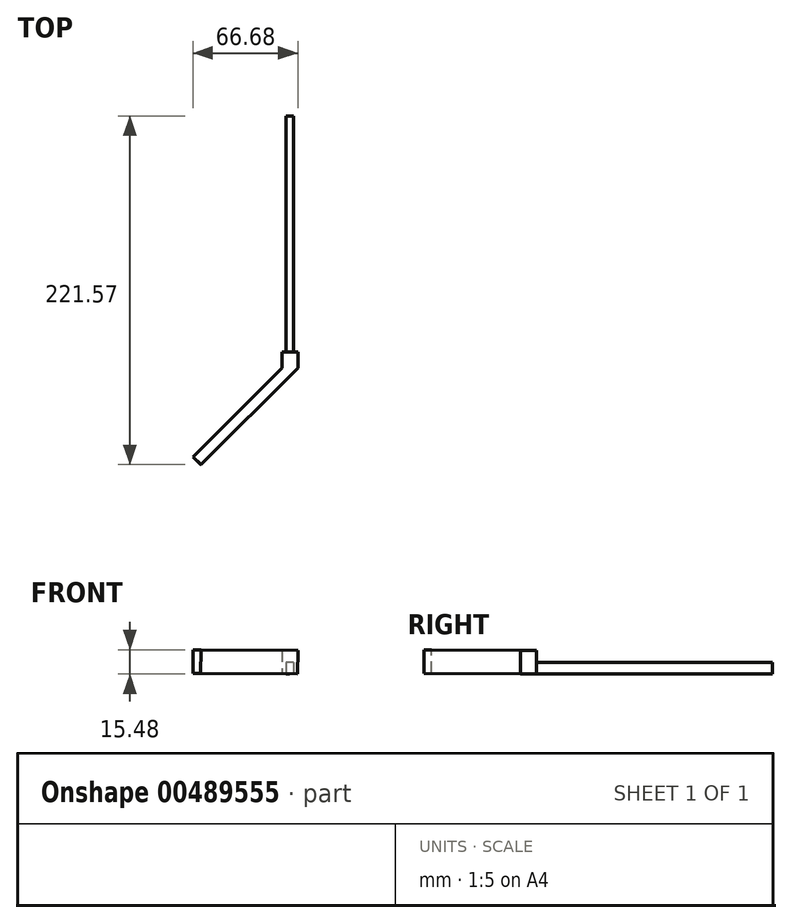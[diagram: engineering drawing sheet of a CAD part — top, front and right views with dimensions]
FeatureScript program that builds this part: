
annotation { "Feature Type Name" : "Feature", "Feature Type Description" : "" }
export const myFeature = defineFeature(function(context is Context, id is Id, definition is map)
    precondition{}
    {
        {
            var Q0;
            Q0=qCreatedBy(makeId("Top.planeOp"),FACE);
            var sketch = newSketch(context, id + "F0", { "sketchPlane" : qUnion([Q0])});
            skLineSegment(sketch, "E0.bottom", {"start": v(2.25, 75) * mm, "end": v(-2.25, 75) * mm});
            skLineSegment(sketch, "E0.top", {"start": v(2.25, -75) * mm, "end": v(-2.25, -75) * mm});
            skLineSegment(sketch, "E0.left", {"start": v(2.25, 75) * mm, "end": v(2.25, -75) * mm});
            skLineSegment(sketch, "E0.right", {"start": v(-2.25, 75) * mm, "end": v(-2.25, -75) * mm});
            skPoint(sketch, "E0.middle", {"position": v(0, 0) * mm});
            skSolve(sketch);
        }
        {
            var Q0;
            Q0 = qSketchRegion(id + "F0", true);
            extrude(context, id + "F1", {"entities" : qUnion([Q0]), "depth" : 7.3 * mm});
        }
        {
            var Q0;
            Q0=makeQuery(id+"F1.opExtrude","SWEPT_FACE",FACE,{"disambiguationData":[OSD([sQuery(id+"F0.wireOp",EDGE,"E0.top")])]});
            var sketch = newSketch(context, id + "F2", { "sketchPlane" : qUnion([Q0])});
            skLineSegment(sketch, "E1.bottom", {"start": v(5.1, 14.96) * mm, "end": v(-4.9, 15.04) * mm});
            skLineSegment(sketch, "E1.left", {"start": v(5.1, 14.96) * mm, "end": v(5, -0.04) * mm});
            skLineSegment(sketch, "E1.right", {"start": v(-4.9, 15.04) * mm, "end": v(-5, 0.04) * mm});
            skPoint(sketch, "E1.middle", {"position": v(0, 0) * mm});
            skLineSegment(sketch, "E2", {"start": v(-5, 0.04) * mm, "end": v(5, -0.04) * mm});
            skPoint(sketch, "E1.top.end.orphan", {"position": v(-5.1, -14.96) * mm});
            skPoint(sketch, "E1.top.start.orphan", {"position": v(4.9, -15.04) * mm});
            skSolve(sketch);
        }
        {
            var Q0;
            {var subQ0=sQuery(id+"F0.wireOp",EDGE,"E0.top");var subQ1=makeQuery(id+"F1.opExtrude","CAP_EDGE",EDGE,{"disambiguationData":[OSD([subQ0])],"isStart":false});Q0=makeQuery(id+"F2.imprint","IMPRINT",FACE,{"disambiguationData":[TD([[makeQuery(id+"F2.imprint","IMPRINT",EDGE,{"derivedFrom":subQ1}),1.0]])]});}
            var Q1;
            Q1=makeQuery(id+"F2.imprint","IMPRINT",FACE,{"disambiguationData":[TD([[makeQuery(id+"F2.imprint","IMPRINT",EDGE,{"derivedFrom":sQuery(id+"F2.wireOp",EDGE,"E1.bottom")}),1.0]])]});
            extrude(context, id + "F3", {"entities" : qUnion([Q0, Q1]), "operationType" : NewBodyOperationType.ADD, "depth" : 10 * mm});
        }
        {
            var Q0;
            Q0=makeQuery(id+"F3.opExtrude","SWEPT_FACE",FACE,{"disambiguationData":[OSD([sQuery(id+"F2.wireOp",EDGE,"E1.bottom")])]});
            var sketch = newSketch(context, id + "F4", { "sketchPlane" : qUnion([Q0])});
            skLineSegment(sketch, "E3", {"start": v(-5, -85) * mm, "end": v(-61.57, -141.57) * mm});
            skLineSegment(sketch, "E4", {"start": v(-56.57, -146.57) * mm, "end": v(5, -85) * mm});
            skLineSegment(sketch, "E5", {"start": v(-61.57, -141.57) * mm, "end": v(-56.57, -146.57) * mm});
            skSolve(sketch);
        }
        {
            var Q0;
            Q0=makeQuery(id+"F4.imprint","IMPRINT",FACE,{"disambiguationData":[TD([[makeQuery(id+"F4.imprint","IMPRINT",EDGE,{"derivedFrom":sQuery(id+"F4.wireOp",EDGE,"E3")}),1.0]])]});
            extrude(context, id + "F5", {"entities" : qUnion([Q0]), "operationType" : NewBodyOperationType.ADD, "oppositeDirection" : true, "depth" : 15 * mm});
        }
    });
